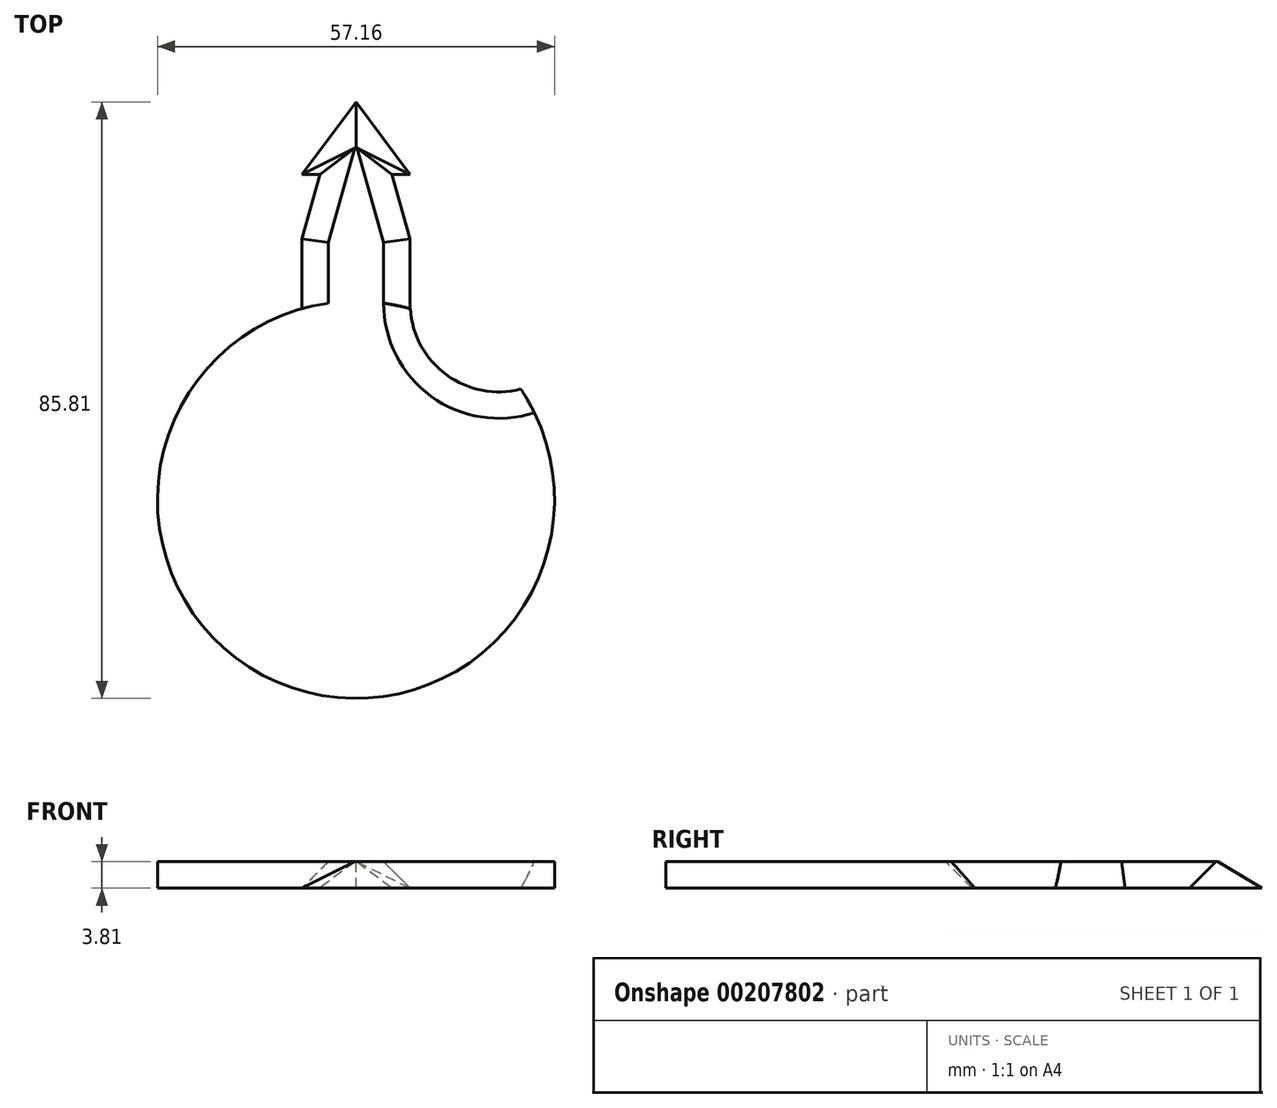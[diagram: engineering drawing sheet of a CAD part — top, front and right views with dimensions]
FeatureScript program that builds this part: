
annotation { "Feature Type Name" : "Feature", "Feature Type Description" : "" }
export const myFeature = defineFeature(function(context is Context, id is Id, definition is map)
    precondition{}
    {
        {
            var Q0;
            Q0=qCreatedBy(makeId("Top.planeOp"),FACE);
            var sketch = newSketch(context, id + "F0", { "sketchPlane" : qUnion([Q0])});
            skCircle(sketch, "E0", {"center": v(0, 0) * mm, "radius": 28.58 * mm});
            skSolve(sketch);
        }
        {
            var Q0;
            Q0=qCreatedBy(makeId("Top.planeOp"),FACE);
            var sketch = newSketch(context, id + "F1", { "sketchPlane" : qUnion([Q0])});
            skLineSegment(sketch, "E1", {"start": v(0, 57.23) * mm, "end": v(-7.8, 46.84) * mm});
            skLineSegment(sketch, "E2", {"start": v(-7.8, 46.84) * mm, "end": v(-5.2, 46.84) * mm});
            skLineSegment(sketch, "E3", {"start": v(-5.2, 46.84) * mm, "end": v(-7.8, 37.57) * mm});
            skLineSegment(sketch, "E4", {"start": v(-7.8, 37.57) * mm, "end": v(-7.8, 24.2) * mm});
            skLineSegment(sketch, "E5.MirrorCS", {"start": v(7.8, 46.84) * mm, "end": v(5.2, 46.84) * mm});
            skLineSegment(sketch, "E6.MirrorCS", {"start": v(5.2, 46.84) * mm, "end": v(7.8, 37.57) * mm});
            skLineSegment(sketch, "E7.MirrorCS", {"start": v(0, 57.23) * mm, "end": v(7.8, 46.84) * mm});
            skLineSegment(sketch, "E8.MirrorCS", {"start": v(7.8, 37.57) * mm, "end": v(7.8, 24.2) * mm});
            skLineSegment(sketch, "E9", {"start": v(-7.8, 24.2) * mm, "end": v(7.8, 24.2) * mm});
            skSolve(sketch);
        }
        {
            var Q0;
            Q0=qCreatedBy(makeId("Front.planeOp"),FACE);
            var sketch = newSketch(context, id + "F2", { "sketchPlane" : qUnion([Q0])});
            skLineSegment(sketch, "E10", {"start": v(0, 0) * mm, "end": v(0, 62.42) * mm, "construction": true});
            skSolve(sketch);
        }
        {
            var Q0;
            Q0 = qSketchRegion(id + "F0", true);
            extrude(context, id + "F3", {"entities" : qUnion([Q0]), "depth" : 3.8 * mm});
        }
        {
            var Q0;
            Q0 = qSketchRegion(id + "F1", true);
            extrude(context, id + "F4", {"entities" : qUnion([Q0]), "operationType" : NewBodyOperationType.ADD, "depth" : 3.8 * mm, "hasDraft" : true, "draftAngle" : 45 * degree, "draftPullDirection" : true});
        }
        {
            var Q0;
            {var subQ0=sQuery(id+"F1.wireOp",EDGE,"E9");var subQ1=sQuery(id+"F1.wireOp",EDGE,"E8.MirrorCS");var subQ2=sQuery(id+"F1.wireOp",EDGE,"E7.MirrorCS");var subQ3=sQuery(id+"F1.wireOp",EDGE,"E6.MirrorCS");var subQ4=sQuery(id+"F1.wireOp",EDGE,"E5.MirrorCS");var subQ5=sQuery(id+"F1.wireOp",EDGE,"E4");var subQ6=sQuery(id+"F1.wireOp",EDGE,"E3");var subQ7=sQuery(id+"F1.wireOp",EDGE,"E2");var subQ8=sQuery(id+"F1.wireOp",EDGE,"E1");Q0=makeQuery(id+"F4YbUptZLWUt5cE_1.4.F4.boolean.opBoolean","MERGE",FACE,{"derivedFrom":[makeQuery(id+"F4YbUptZLWUt5cE_1.3.F4.boolean.opBoolean","MERGE",FACE,{"derivedFrom":[makeQuery(id+"F4YbUptZLWUt5cE_1.2.F4.boolean.opBoolean","MERGE",FACE,{"derivedFrom":[makeQuery(id+"F4YbUptZLWUt5cE_1.1.F4.boolean.opBoolean","MERGE",FACE,{"derivedFrom":[makeQuery(id+"F4.boolean.opBoolean","MERGE",FACE,{"derivedFrom":[makeQuery(id+"F3.opExtrude","CAP_FACE",FACE,{"disambiguationData":[OSD([sQuery(id+"F0.wireOp",EDGE,"E0")])],"isStart":false}),makeQuery(id+"F4.opExtrude","CAP_FACE",FACE,{"disambiguationData":[OSD([subQ8,subQ7,subQ6,subQ5,subQ4,subQ3,subQ2,subQ1,subQ0])],"isStart":false})]}),makeQuery(id+"F4YbUptZLWUt5cE_1.1.F4.opExtrude","CAP_FACE",FACE,{"disambiguationData":[OSD([subQ8,subQ7,subQ6,subQ5,subQ4,subQ3,subQ2,subQ1,subQ0])],"isStart":false})]}),makeQuery(id+"F4YbUptZLWUt5cE_1.2.F4.opExtrude","CAP_FACE",FACE,{"disambiguationData":[OSD([subQ8,subQ7,subQ6,subQ5,subQ4,subQ3,subQ2,subQ1,subQ0])],"isStart":false})]}),makeQuery(id+"F4YbUptZLWUt5cE_1.3.F4.opExtrude","CAP_FACE",FACE,{"disambiguationData":[OSD([subQ8,subQ7,subQ6,subQ5,subQ4,subQ3,subQ2,subQ1,subQ0])],"isStart":false})]}),makeQuery(id+"F4YbUptZLWUt5cE_1.4.F4.opExtrude","CAP_FACE",FACE,{"disambiguationData":[OSD([subQ8,subQ7,subQ6,subQ5,subQ4,subQ3,subQ2,subQ1,subQ0])],"isStart":false})]});}
            var sketch = newSketch(context, id + "F5", { "sketchPlane" : qUnion([Q0])});
            skArc(sketch, "E11", {"start": v(3.98, 28.3) * mm, "mid": v(10.81, 14.89) * mm, "end": v(25.68, 12.53) * mm});
            skArc(sketch, "E12", {"start": v(25.68, 12.53) * mm, "mid": v(25.03, 34.46) * mm, "end": v(3.98, 28.3) * mm});
            skSolve(sketch);
        }
        {
            var Q0;
            Q0 = qSketchRegion(id + "F5", true);
            extrude(context, id + "F6", {"entities" : qUnion([Q0]), "operationType" : NewBodyOperationType.REMOVE, "oppositeDirection" : true, "depth" : 3.8 * mm, "hasDraft" : true, "draftAngle" : 45 * degree, "draftPullDirection" : true});
        }
    });
